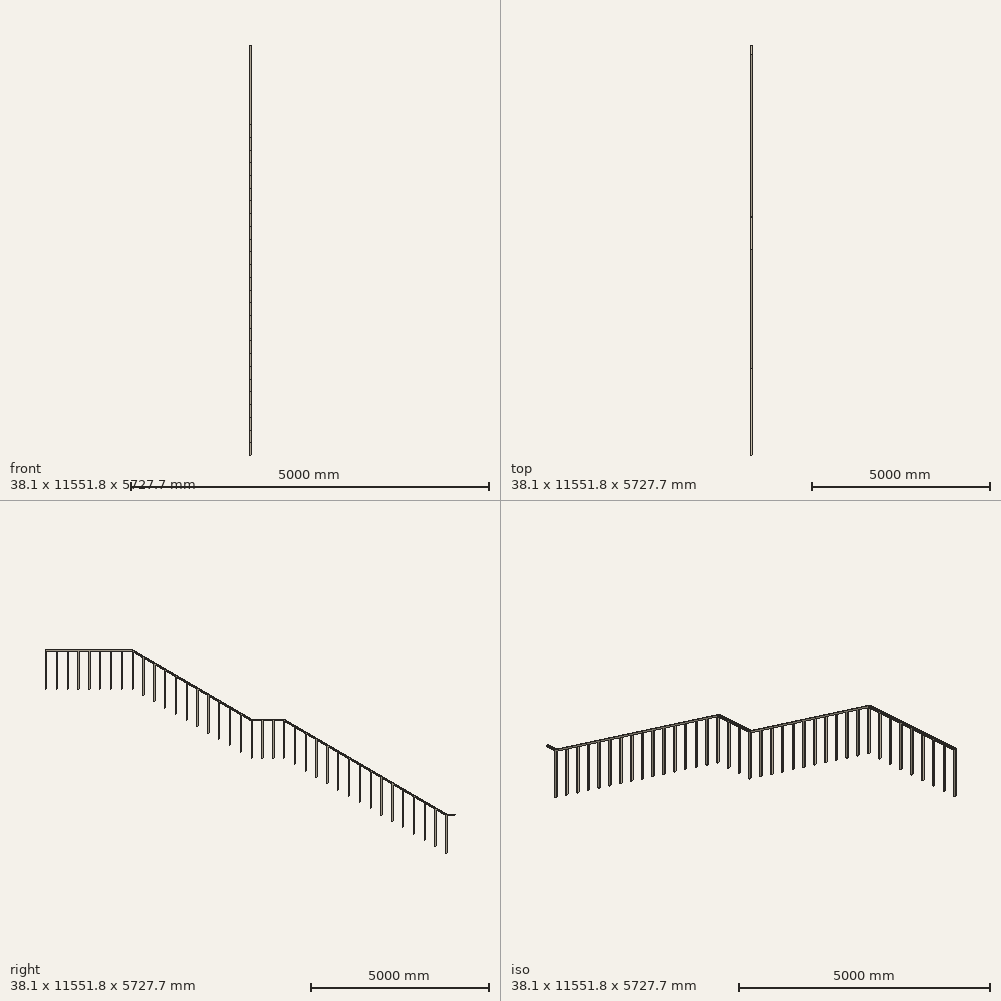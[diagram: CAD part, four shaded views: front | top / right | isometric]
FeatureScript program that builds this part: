
annotation { "Feature Type Name" : "Feature", "Feature Type Description" : "" }
export const myFeature = defineFeature(function(context is Context, id is Id, definition is map)
    precondition{}
    {
        {
            var Q0;
            Q0=qCreatedBy(makeId("Right.planeOp"),FACE);
            var sketch = newSketch(context, id + "F0", { "sketchPlane" : qUnion([Q0])});
            skLineSegment(sketch, "E0.bottom", {"start": v(0, 0) * mm, "end": v(-38.1, 0) * mm});
            skLineSegment(sketch, "E0.top", {"start": v(0, 1066.8) * mm, "end": v(-38.1, 1066.8) * mm});
            skLineSegment(sketch, "E0.left", {"start": v(0, 0) * mm, "end": v(0, 1066.8) * mm});
            skLineSegment(sketch, "E0.right", {"start": v(-38.1, 0) * mm, "end": v(-38.1, 1066.8) * mm});
            skLineSegment(sketch, "E1.bottom", {"start": v(-304.8, 1244.6) * mm, "end": v(-342.9, 1244.6) * mm});
            skLineSegment(sketch, "E1.top", {"start": v(-304.8, 177.8) * mm, "end": v(-342.9, 177.8) * mm});
            skLineSegment(sketch, "E1.left", {"start": v(-304.8, 1244.6) * mm, "end": v(-304.8, 177.8) * mm});
            skLineSegment(sketch, "E1.right", {"start": v(-342.9, 1244.6) * mm, "end": v(-342.9, 177.8) * mm});
            skLineSegment(sketch, "E2.bottom", {"start": v(-609.6, 1422.4) * mm, "end": v(-647.7, 1422.4) * mm});
            skLineSegment(sketch, "E2.top", {"start": v(-609.6, 355.6) * mm, "end": v(-647.7, 355.6) * mm});
            skLineSegment(sketch, "E2.left", {"start": v(-609.6, 1422.4) * mm, "end": v(-609.6, 355.6) * mm});
            skLineSegment(sketch, "E2.right", {"start": v(-647.7, 1422.4) * mm, "end": v(-647.7, 355.6) * mm});
            skLineSegment(sketch, "E3.bottom", {"start": v(-914.4, 1600.2) * mm, "end": v(-952.5, 1600.2) * mm});
            skLineSegment(sketch, "E3.top", {"start": v(-914.4, 533.4) * mm, "end": v(-952.5, 533.4) * mm});
            skLineSegment(sketch, "E3.left", {"start": v(-914.4, 1600.2) * mm, "end": v(-914.4, 533.4) * mm});
            skLineSegment(sketch, "E3.right", {"start": v(-952.5, 1600.2) * mm, "end": v(-952.5, 533.4) * mm});
            skLineSegment(sketch, "E4.bottom", {"start": v(-1219.2, 1778) * mm, "end": v(-1257.3, 1778) * mm});
            skLineSegment(sketch, "E4.top", {"start": v(-1219.2, 711.2) * mm, "end": v(-1257.3, 711.2) * mm});
            skLineSegment(sketch, "E4.left", {"start": v(-1219.2, 1778) * mm, "end": v(-1219.2, 711.2) * mm});
            skLineSegment(sketch, "E4.right", {"start": v(-1257.3, 1778) * mm, "end": v(-1257.3, 711.2) * mm});
            skLineSegment(sketch, "E5.bottom", {"start": v(-1524, 889) * mm, "end": v(-1562.1, 889) * mm});
            skLineSegment(sketch, "E5.top", {"start": v(-1524, 1955.8) * mm, "end": v(-1562.1, 1955.8) * mm});
            skLineSegment(sketch, "E5.left", {"start": v(-1524, 889) * mm, "end": v(-1524, 1955.8) * mm});
            skLineSegment(sketch, "E5.right", {"start": v(-1562.1, 889) * mm, "end": v(-1562.1, 1955.8) * mm});
            skLineSegment(sketch, "E6.bottom", {"start": v(-1828.8, 1066.8) * mm, "end": v(-1866.9, 1066.8) * mm});
            skLineSegment(sketch, "E6.top", {"start": v(-1828.8, 2133.6) * mm, "end": v(-1866.9, 2133.6) * mm});
            skLineSegment(sketch, "E6.left", {"start": v(-1828.8, 1066.8) * mm, "end": v(-1828.8, 2133.6) * mm});
            skLineSegment(sketch, "E6.right", {"start": v(-1866.9, 1066.8) * mm, "end": v(-1866.9, 2133.6) * mm});
            skLineSegment(sketch, "E7.bottom", {"start": v(-2133.6, 1244.6) * mm, "end": v(-2171.7, 1244.6) * mm});
            skLineSegment(sketch, "E7.top", {"start": v(-2133.6, 2311.4) * mm, "end": v(-2171.7, 2311.4) * mm});
            skLineSegment(sketch, "E7.left", {"start": v(-2133.6, 1244.6) * mm, "end": v(-2133.6, 2311.4) * mm});
            skLineSegment(sketch, "E7.right", {"start": v(-2171.7, 1244.6) * mm, "end": v(-2171.7, 2311.4) * mm});
            skLineSegment(sketch, "E8.right", {"start": v(-3390.9, 3022.6) * mm, "end": v(-3390.9, 1955.8) * mm});
            skLineSegment(sketch, "E9.right", {"start": v(-3086.1, 2844.8) * mm, "end": v(-3086.1, 1778) * mm});
            skLineSegment(sketch, "E10.right", {"start": v(-4000.5, 2311.4) * mm, "end": v(-4000.5, 3378.2) * mm});
            skLineSegment(sketch, "E11.right", {"start": v(-3695.7, 2133.6) * mm, "end": v(-3695.7, 3200.4) * mm});
            skLineSegment(sketch, "E9.left", {"start": v(-3048, 2844.8) * mm, "end": v(-3048, 1778) * mm});
            skLineSegment(sketch, "E12.left", {"start": v(-4267.2, 2489.2) * mm, "end": v(-4267.2, 3556) * mm});
            skLineSegment(sketch, "E13.right", {"start": v(-2781.3, 2667) * mm, "end": v(-2781.3, 1600.2) * mm});
            skLineSegment(sketch, "E13.left", {"start": v(-2743.2, 2667) * mm, "end": v(-2743.2, 1600.2) * mm});
            skLineSegment(sketch, "E14.right", {"start": v(-2476.5, 2489.2) * mm, "end": v(-2476.5, 1422.4) * mm});
            skLineSegment(sketch, "E10.left", {"start": v(-3962.4, 2311.4) * mm, "end": v(-3962.4, 3378.2) * mm});
            skLineSegment(sketch, "E14.left", {"start": v(-2438.4, 2489.2) * mm, "end": v(-2438.4, 1422.4) * mm});
            skLineSegment(sketch, "E11.left", {"start": v(-3657.6, 2133.6) * mm, "end": v(-3657.6, 3200.4) * mm});
            skLineSegment(sketch, "E12.right", {"start": v(-4305.3, 2489.2) * mm, "end": v(-4305.3, 3556) * mm});
            skLineSegment(sketch, "E8.left", {"start": v(-3352.8, 3022.6) * mm, "end": v(-3352.8, 1955.8) * mm});
            skLineSegment(sketch, "E11.bottom", {"start": v(-3657.6, 2133.6) * mm, "end": v(-3695.7, 2133.6) * mm});
            skLineSegment(sketch, "E8.bottom", {"start": v(-3352.8, 3022.6) * mm, "end": v(-3390.9, 3022.6) * mm});
            skLineSegment(sketch, "E12.bottom", {"start": v(-4267.2, 2489.2) * mm, "end": v(-4305.3, 2489.2) * mm});
            skLineSegment(sketch, "E12.top", {"start": v(-4267.2, 3556) * mm, "end": v(-4305.3, 3556) * mm});
            skLineSegment(sketch, "E10.bottom", {"start": v(-3962.4, 2311.4) * mm, "end": v(-4000.5, 2311.4) * mm});
            skLineSegment(sketch, "E9.bottom", {"start": v(-3048, 2844.8) * mm, "end": v(-3086.1, 2844.8) * mm});
            skLineSegment(sketch, "E9.top", {"start": v(-3048, 1778) * mm, "end": v(-3086.1, 1778) * mm});
            skLineSegment(sketch, "E11.top", {"start": v(-3657.6, 3200.4) * mm, "end": v(-3695.7, 3200.4) * mm});
            skLineSegment(sketch, "E8.top", {"start": v(-3352.8, 1955.8) * mm, "end": v(-3390.9, 1955.8) * mm});
            skLineSegment(sketch, "E13.top", {"start": v(-2743.2, 1600.2) * mm, "end": v(-2781.3, 1600.2) * mm});
            skLineSegment(sketch, "E13.bottom", {"start": v(-2743.2, 2667) * mm, "end": v(-2781.3, 2667) * mm});
            skLineSegment(sketch, "E14.bottom", {"start": v(-2438.4, 2489.2) * mm, "end": v(-2476.5, 2489.2) * mm});
            skLineSegment(sketch, "E14.top", {"start": v(-2438.4, 1422.4) * mm, "end": v(-2476.5, 1422.4) * mm});
            skLineSegment(sketch, "E10.top", {"start": v(-3962.4, 3378.2) * mm, "end": v(-4000.5, 3378.2) * mm});
            skLineSegment(sketch, "E15.right", {"start": v(-5524.5, 3733.8) * mm, "end": v(-5524.5, 2667) * mm});
            skLineSegment(sketch, "E16.right", {"start": v(-5219.7, 3733.8) * mm, "end": v(-5219.7, 2667) * mm});
            skLineSegment(sketch, "E17.right", {"start": v(-6134.1, 3022.6) * mm, "end": v(-6134.1, 4089.4) * mm});
            skLineSegment(sketch, "E18.right", {"start": v(-5829.3, 2844.8) * mm, "end": v(-5829.3, 3911.6) * mm});
            skLineSegment(sketch, "E16.left", {"start": v(-5181.6, 3733.8) * mm, "end": v(-5181.6, 2667) * mm});
            skLineSegment(sketch, "E19.left", {"start": v(-6400.8, 3200.4) * mm, "end": v(-6400.8, 4267.2) * mm});
            skLineSegment(sketch, "E20.right", {"start": v(-4914.9, 3733.8) * mm, "end": v(-4914.9, 2667) * mm});
            skLineSegment(sketch, "E20.left", {"start": v(-4876.8, 3733.8) * mm, "end": v(-4876.8, 2667) * mm});
            skLineSegment(sketch, "E21.right", {"start": v(-4610.1, 3733.8) * mm, "end": v(-4610.1, 2667) * mm});
            skLineSegment(sketch, "E17.left", {"start": v(-6096, 3022.6) * mm, "end": v(-6096, 4089.4) * mm});
            skLineSegment(sketch, "E21.left", {"start": v(-4572, 3733.8) * mm, "end": v(-4572, 2667) * mm});
            skLineSegment(sketch, "E18.left", {"start": v(-5791.2, 2844.8) * mm, "end": v(-5791.2, 3911.6) * mm});
            skLineSegment(sketch, "E19.right", {"start": v(-6438.9, 3200.4) * mm, "end": v(-6438.9, 4267.2) * mm});
            skLineSegment(sketch, "E15.left", {"start": v(-5486.4, 3733.8) * mm, "end": v(-5486.4, 2667) * mm});
            skLineSegment(sketch, "E18.bottom", {"start": v(-5791.2, 2844.8) * mm, "end": v(-5829.3, 2844.8) * mm});
            skLineSegment(sketch, "E15.bottom", {"start": v(-5486.4, 3733.8) * mm, "end": v(-5524.5, 3733.8) * mm});
            skLineSegment(sketch, "E19.bottom", {"start": v(-6400.8, 3200.4) * mm, "end": v(-6438.9, 3200.4) * mm});
            skLineSegment(sketch, "E19.top", {"start": v(-6400.8, 4267.2) * mm, "end": v(-6438.9, 4267.2) * mm});
            skLineSegment(sketch, "E17.bottom", {"start": v(-6096, 3022.6) * mm, "end": v(-6134.1, 3022.6) * mm});
            skLineSegment(sketch, "E16.bottom", {"start": v(-5181.6, 3733.8) * mm, "end": v(-5219.7, 3733.8) * mm});
            skLineSegment(sketch, "E16.top", {"start": v(-5181.6, 2667) * mm, "end": v(-5219.7, 2667) * mm});
            skLineSegment(sketch, "E18.top", {"start": v(-5791.2, 3911.6) * mm, "end": v(-5829.3, 3911.6) * mm});
            skLineSegment(sketch, "E15.top", {"start": v(-5486.4, 2667) * mm, "end": v(-5524.5, 2667) * mm});
            skLineSegment(sketch, "E20.top", {"start": v(-4876.8, 2667) * mm, "end": v(-4914.9, 2667) * mm});
            skLineSegment(sketch, "E20.bottom", {"start": v(-4876.8, 3733.8) * mm, "end": v(-4914.9, 3733.8) * mm});
            skLineSegment(sketch, "E21.bottom", {"start": v(-4572, 3733.8) * mm, "end": v(-4610.1, 3733.8) * mm});
            skLineSegment(sketch, "E21.top", {"start": v(-4572, 2667) * mm, "end": v(-4610.1, 2667) * mm});
            skLineSegment(sketch, "E17.top", {"start": v(-6096, 4089.4) * mm, "end": v(-6134.1, 4089.4) * mm});
            skLineSegment(sketch, "E22.left", {"start": v(-7010.4, 3556) * mm, "end": v(-7010.4, 4622.8) * mm});
            skLineSegment(sketch, "E23.right", {"start": v(-7658.1, 4978.4) * mm, "end": v(-7658.1, 3911.6) * mm});
            skLineSegment(sketch, "E22.right", {"start": v(-7048.5, 3556) * mm, "end": v(-7048.5, 4622.8) * mm});
            skLineSegment(sketch, "E23.left", {"start": v(-7620, 4978.4) * mm, "end": v(-7620, 3911.6) * mm});
            skLineSegment(sketch, "E24.right", {"start": v(-8267.7, 5334) * mm, "end": v(-8267.7, 4267.2) * mm});
            skLineSegment(sketch, "E25.right", {"start": v(-7353.3, 4800.6) * mm, "end": v(-7353.3, 3733.8) * mm});
            skLineSegment(sketch, "E26.right", {"start": v(-7962.9, 5156.2) * mm, "end": v(-7962.9, 4089.4) * mm});
            skLineSegment(sketch, "E27.left", {"start": v(-8839.2, 4622.8) * mm, "end": v(-8839.2, 5689.6) * mm});
            skLineSegment(sketch, "E27.right", {"start": v(-8877.3, 4622.8) * mm, "end": v(-8877.3, 5689.6) * mm});
            skLineSegment(sketch, "E26.left", {"start": v(-7924.8, 5156.2) * mm, "end": v(-7924.8, 4089.4) * mm});
            skLineSegment(sketch, "E24.left", {"start": v(-8229.6, 5334) * mm, "end": v(-8229.6, 4267.2) * mm});
            skLineSegment(sketch, "E28.right", {"start": v(-6743.7, 3378.2) * mm, "end": v(-6743.7, 4445) * mm});
            skLineSegment(sketch, "E29.left", {"start": v(-8534.4, 4445) * mm, "end": v(-8534.4, 5511.8) * mm});
            skLineSegment(sketch, "E29.right", {"start": v(-8572.5, 4445) * mm, "end": v(-8572.5, 5511.8) * mm});
            skLineSegment(sketch, "E28.left", {"start": v(-6705.6, 3378.2) * mm, "end": v(-6705.6, 4445) * mm});
            skLineSegment(sketch, "E25.left", {"start": v(-7315.2, 4800.6) * mm, "end": v(-7315.2, 3733.8) * mm});
            skLineSegment(sketch, "E29.top", {"start": v(-8534.4, 5511.8) * mm, "end": v(-8572.5, 5511.8) * mm});
            skLineSegment(sketch, "E29.bottom", {"start": v(-8534.4, 4445) * mm, "end": v(-8572.5, 4445) * mm});
            skLineSegment(sketch, "E24.bottom", {"start": v(-8229.6, 5334) * mm, "end": v(-8267.7, 5334) * mm});
            skLineSegment(sketch, "E24.top", {"start": v(-8229.6, 4267.2) * mm, "end": v(-8267.7, 4267.2) * mm});
            skLineSegment(sketch, "E22.bottom", {"start": v(-7010.4, 3556) * mm, "end": v(-7048.5, 3556) * mm});
            skLineSegment(sketch, "E23.top", {"start": v(-7620, 3911.6) * mm, "end": v(-7658.1, 3911.6) * mm});
            skLineSegment(sketch, "E23.bottom", {"start": v(-7620, 4978.4) * mm, "end": v(-7658.1, 4978.4) * mm});
            skLineSegment(sketch, "E28.bottom", {"start": v(-6705.6, 3378.2) * mm, "end": v(-6743.7, 3378.2) * mm});
            skLineSegment(sketch, "E25.bottom", {"start": v(-7315.2, 4800.6) * mm, "end": v(-7353.3, 4800.6) * mm});
            skLineSegment(sketch, "E28.top", {"start": v(-6705.6, 4445) * mm, "end": v(-6743.7, 4445) * mm});
            skLineSegment(sketch, "E27.bottom", {"start": v(-8839.2, 4622.8) * mm, "end": v(-8877.3, 4622.8) * mm});
            skLineSegment(sketch, "E22.top", {"start": v(-7010.4, 4622.8) * mm, "end": v(-7048.5, 4622.8) * mm});
            skLineSegment(sketch, "E26.top", {"start": v(-7924.8, 4089.4) * mm, "end": v(-7962.9, 4089.4) * mm});
            skLineSegment(sketch, "E27.top", {"start": v(-8839.2, 5689.6) * mm, "end": v(-8877.3, 5689.6) * mm});
            skLineSegment(sketch, "E26.bottom", {"start": v(-7924.8, 5156.2) * mm, "end": v(-7962.9, 5156.2) * mm});
            skLineSegment(sketch, "E25.top", {"start": v(-7315.2, 3733.8) * mm, "end": v(-7353.3, 3733.8) * mm});
            skLineSegment(sketch, "E30.right", {"start": v(-10096.5, 5689.6) * mm, "end": v(-10096.5, 4622.8) * mm});
            skLineSegment(sketch, "E31.left", {"start": v(-9144, 5689.6) * mm, "end": v(-9144, 4622.8) * mm});
            skLineSegment(sketch, "E31.right", {"start": v(-9182.1, 5689.6) * mm, "end": v(-9182.1, 4622.8) * mm});
            skLineSegment(sketch, "E32.right", {"start": v(-9791.7, 5689.6) * mm, "end": v(-9791.7, 4622.8) * mm});
            skLineSegment(sketch, "E33.left", {"start": v(-9448.8, 5689.6) * mm, "end": v(-9448.8, 4622.8) * mm});
            skLineSegment(sketch, "E30.left", {"start": v(-10058.4, 5689.6) * mm, "end": v(-10058.4, 4622.8) * mm});
            skLineSegment(sketch, "E32.left", {"start": v(-9753.6, 5689.6) * mm, "end": v(-9753.6, 4622.8) * mm});
            skLineSegment(sketch, "E33.right", {"start": v(-9486.9, 5689.6) * mm, "end": v(-9486.9, 4622.8) * mm});
            skLineSegment(sketch, "E31.bottom", {"start": v(-9144, 5689.6) * mm, "end": v(-9182.1, 5689.6) * mm});
            skLineSegment(sketch, "E31.top", {"start": v(-9144, 4622.8) * mm, "end": v(-9182.1, 4622.8) * mm});
            skLineSegment(sketch, "E33.bottom", {"start": v(-9448.8, 5689.6) * mm, "end": v(-9486.9, 5689.6) * mm});
            skLineSegment(sketch, "E33.top", {"start": v(-9448.8, 4622.8) * mm, "end": v(-9486.9, 4622.8) * mm});
            skLineSegment(sketch, "E30.bottom", {"start": v(-10058.4, 5689.6) * mm, "end": v(-10096.5, 5689.6) * mm});
            skLineSegment(sketch, "E32.bottom", {"start": v(-9753.6, 5689.6) * mm, "end": v(-9791.7, 5689.6) * mm});
            skLineSegment(sketch, "E32.top", {"start": v(-9753.6, 4622.8) * mm, "end": v(-9791.7, 4622.8) * mm});
            skLineSegment(sketch, "E30.top", {"start": v(-10058.4, 4622.8) * mm, "end": v(-10096.5, 4622.8) * mm});
            skLineSegment(sketch, "E34.right", {"start": v(-11315.7, 5689.6) * mm, "end": v(-11315.7, 4622.8) * mm});
            skLineSegment(sketch, "E35.left", {"start": v(-10363.2, 5689.6) * mm, "end": v(-10363.2, 4622.8) * mm});
            skLineSegment(sketch, "E35.right", {"start": v(-10401.3, 5689.6) * mm, "end": v(-10401.3, 4622.8) * mm});
            skLineSegment(sketch, "E36.right", {"start": v(-11010.9, 5689.6) * mm, "end": v(-11010.9, 4622.8) * mm});
            skLineSegment(sketch, "E37.left", {"start": v(-10668, 5689.6) * mm, "end": v(-10668, 4622.8) * mm});
            skLineSegment(sketch, "E34.left", {"start": v(-11277.6, 5689.6) * mm, "end": v(-11277.6, 4622.8) * mm});
            skLineSegment(sketch, "E36.left", {"start": v(-10972.8, 5689.6) * mm, "end": v(-10972.8, 4622.8) * mm});
            skLineSegment(sketch, "E37.right", {"start": v(-10706.1, 5689.6) * mm, "end": v(-10706.1, 4622.8) * mm});
            skLineSegment(sketch, "E35.bottom", {"start": v(-10363.2, 5689.6) * mm, "end": v(-10401.3, 5689.6) * mm});
            skLineSegment(sketch, "E35.top", {"start": v(-10363.2, 4622.8) * mm, "end": v(-10401.3, 4622.8) * mm});
            skLineSegment(sketch, "E37.bottom", {"start": v(-10668, 5689.6) * mm, "end": v(-10706.1, 5689.6) * mm});
            skLineSegment(sketch, "E37.top", {"start": v(-10668, 4622.8) * mm, "end": v(-10706.1, 4622.8) * mm});
            skLineSegment(sketch, "E34.bottom", {"start": v(-11277.6, 5689.6) * mm, "end": v(-11315.7, 5689.6) * mm});
            skLineSegment(sketch, "E36.bottom", {"start": v(-10972.8, 5689.6) * mm, "end": v(-11010.9, 5689.6) * mm});
            skLineSegment(sketch, "E36.top", {"start": v(-10972.8, 4622.8) * mm, "end": v(-11010.9, 4622.8) * mm});
            skLineSegment(sketch, "E34.top", {"start": v(-11277.6, 4622.8) * mm, "end": v(-11315.7, 4622.8) * mm});
            skLineSegment(sketch, "E38", {"start": v(236.07, 1066.8) * mm, "end": v(-38.1, 1066.8) * mm});
            skLineSegment(sketch, "E39", {"start": v(-4610.1, 3733.8) * mm, "end": v(-38.1, 1066.8) * mm});
            skLineSegment(sketch, "E40", {"start": v(-4610.1, 3733.8) * mm, "end": v(-5524.5, 3733.8) * mm});
            skLineSegment(sketch, "E41", {"start": v(-5524.5, 3733.8) * mm, "end": v(-8877.3, 5689.6) * mm});
            skLineSegment(sketch, "E42", {"start": v(-8877.3, 5689.6) * mm, "end": v(-11315.7, 5689.6) * mm});
            skLineSegment(sketch, "E43.0", {"start": v(-8877.3, 5727.7) * mm, "end": v(-11315.7, 5727.7) * mm});
            skLineSegment(sketch, "E44.0", {"start": v(-5514.2, 3771.9) * mm, "end": v(-8858.1, 5722.5) * mm});
            skLineSegment(sketch, "E45.0", {"start": v(-4610.1, 3771.9) * mm, "end": v(-5514.2, 3771.9) * mm});
            skLineSegment(sketch, "E46.0", {"start": v(-4590.9, 3766.7) * mm, "end": v(-18.9, 1099.7) * mm});
            skLineSegment(sketch, "E47", {"start": v(-18.9, 1099.7) * mm, "end": v(236.07, 1099.7) * mm});
            skLineSegment(sketch, "E48", {"start": v(236.07, 1099.7) * mm, "end": v(236.07, 1066.8) * mm});
            skLineSegment(sketch, "E49", {"start": v(-4610.1, 3771.9) * mm, "end": v(-4590.9, 3766.7) * mm});
            skLineSegment(sketch, "E50", {"start": v(-8877.3, 5727.7) * mm, "end": v(-8858.1, 5722.5) * mm});
            skLineSegment(sketch, "E51", {"start": v(-11315.7, 5727.7) * mm, "end": v(-11315.7, 5689.6) * mm});
            skSolve(sketch);
        }
        {
            var Q0;
            Q0 = qSketchRegion(id + "F0", true);
            extrude(context, id + "F1", {"entities" : qUnion([Q0]), "depth" : 38.1 * mm});
        }
    });
